# Revit family: ok-Celite_Uso Geral_Bacia Infantil_08254
name_source: partatom
category: Plumbing Fixtures
revit_build: Autodesk Revit MEP 2014 (Build: 20131024_2115(x64)
units: mm (PartAtom-declared; Revit-internal decimal feet)

## types (1)
- Branca - 08254
    Assembly Code = D2010100
    Bolsa para bacia = Bolsa tubo para bacia convencional (00638), Acessórios - Metais Celite
    CWFU = 1
    Celite: Categoria = Uso Geral
    Celite: Cores Disponíveis = Água marinha
    Celite: Código = 08254
    Celite: Descrição = Bacia convencional cor água branca (08254), linha Infantil - Louças Celite
    Celite: Desenho Técnico = http://www.celite.com.br
    Celite: Fabricante = Celite
    Celite: Linha = Infantil
    Celite: Link do Produto = http://www.celite.com.br
    Celite: Norma = ABNT NBR 15097-1: 2011 / ABNT NBR 15097-2: 2011 - fabricação/instalação
    Celite: Produto = Louças
    Celite: Tipo = Bacias convencionais
    Celite: Versão = Autodesk Revit MEP 2014
    Default Elevation = 0 m
    Description = Bacia convencional cor água branca (08254), linha Infantil - Louças Celite
    Desenvolvido por = ofcdesk
    Diâmetro Ponto de Esgoto = 100 mm
    Manufacturer = Celite
    Model = 08254
    Raio Ponto de Esgoto = 50 mm
    Raio Ponto de Água = 20 mm
    Selo de Qualidade ofcdesk = Standard
    URL = http://www.celite.com.br
    WFU = 3

## geometry (parser evidence)
native form markers: Blend x4, Sweep x9
no freeform markers — native parametric forms only
